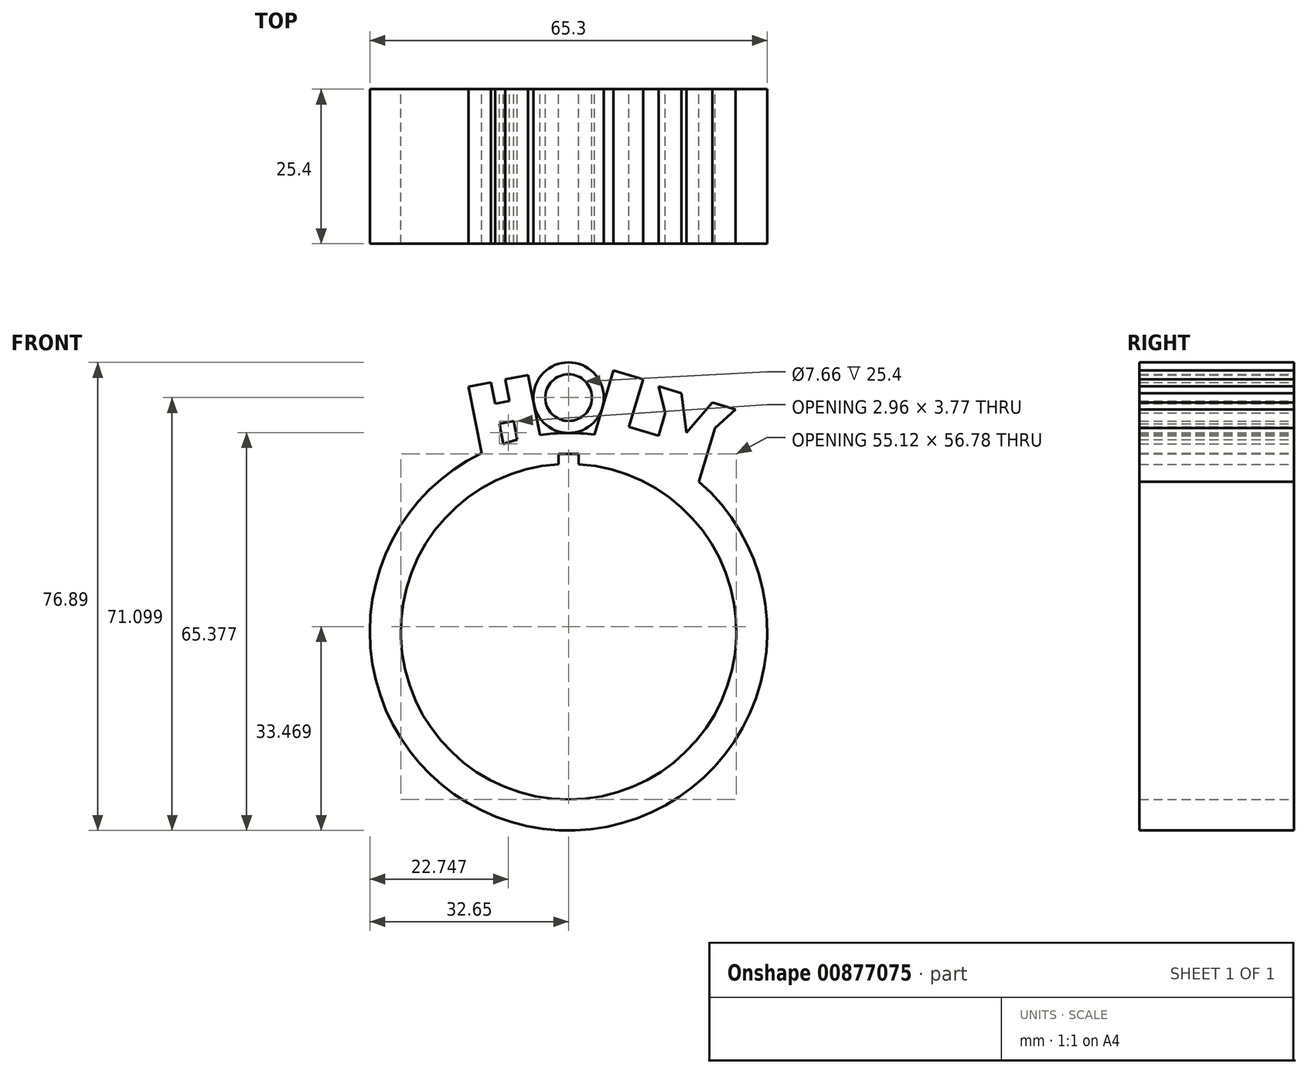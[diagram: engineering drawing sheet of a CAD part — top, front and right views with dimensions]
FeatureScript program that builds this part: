
annotation { "Feature Type Name" : "Feature", "Feature Type Description" : "" }
export const myFeature = defineFeature(function(context is Context, id is Id, definition is map)
    precondition{}
    {
        {
            var Q0;
            Q0=qCreatedBy(makeId("Front.planeOp"),FACE);
            var sketch = newSketch(context, id + "F0", { "sketchPlane" : qUnion([Q0])});
            skLineSegment(sketch, "E0", {"start": v(0, -38.5) * mm, "end": v(0, 44.83) * mm, "construction": true});
            skCircle(sketch, "E1", {"center": v(0, 0) * mm, "radius": 27.57 * mm});
            skArc(sketch, "E2", {"start": v(17.77, 27.4) * mm, "mid": v(-18.57, -26.86) * mm, "end": v(19.34, 26.3) * mm});
            skLineSegment(sketch, "E3", {"start": v(-16.47, 40.24) * mm, "end": v(-14.31, 29.35) * mm});
            skLineSegment(sketch, "E4", {"start": v(-16.47, 40.24) * mm, "end": v(-12.74, 40.98) * mm});
            skLineSegment(sketch, "E5", {"start": v(-12.74, 40.98) * mm, "end": v(-12.04, 37.45) * mm});
            skLineSegment(sketch, "E6", {"start": v(-12.04, 37.45) * mm, "end": v(-9.69, 37.92) * mm});
            skLineSegment(sketch, "E7", {"start": v(-9.69, 37.92) * mm, "end": v(-10.39, 41.44) * mm});
            skLineSegment(sketch, "E8", {"start": v(-10.39, 41.44) * mm, "end": v(-6.65, 42.18) * mm});
            skLineSegment(sketch, "E9", {"start": v(-6.65, 42.18) * mm, "end": v(-4.7, 32.31) * mm});
            skLineSegment(sketch, "E10", {"start": v(-11.38, 34.15) * mm, "end": v(-10.73, 30.84) * mm});
            skLineSegment(sketch, "E11", {"start": v(-11.38, 34.15) * mm, "end": v(-9.03, 34.61) * mm});
            skLineSegment(sketch, "E12", {"start": v(-9.03, 34.61) * mm, "end": v(-8.42, 31.55) * mm});
            skCircle(sketch, "E13", {"center": v(0, 38.45) * mm, "radius": 5.8 * mm});
            skCircle(sketch, "E14", {"center": v(0, 38.45) * mm, "radius": 3.83 * mm});
            skLineSegment(sketch, "E15", {"start": v(7.4, 42.9) * mm, "end": v(4.22, 32.38) * mm});
            skLineSegment(sketch, "E16", {"start": v(7.4, 42.9) * mm, "end": v(12.26, 41.43) * mm});
            skLineSegment(sketch, "E17", {"start": v(12.26, 41.43) * mm, "end": v(9.92, 33.67) * mm});
            skLineSegment(sketch, "E18", {"start": v(9.92, 33.67) * mm, "end": v(14.78, 32.2) * mm});
            skLineSegment(sketch, "E19", {"start": v(14.78, 32.2) * mm, "end": v(13.97, 29.51) * mm});
            skLineSegment(sketch, "E20", {"start": v(17.77, 27.4) * mm, "end": v(19.34, 26.3) * mm});
            skLineSegment(sketch, "E21", {"start": v(14.78, 32.2) * mm, "end": v(15.9, 35.9) * mm});
            skLineSegment(sketch, "E22", {"start": v(15.9, 35.9) * mm, "end": v(14.78, 40.33) * mm});
            skLineSegment(sketch, "E23", {"start": v(14.78, 40.33) * mm, "end": v(18.55, 39.2) * mm});
            skLineSegment(sketch, "E24", {"start": v(18.55, 39.2) * mm, "end": v(19.37, 32.67) * mm});
            skLineSegment(sketch, "E25", {"start": v(19.37, 32.67) * mm, "end": v(17.77, 27.4) * mm, "construction": true});
            skLineSegment(sketch, "E26.MirrorCS", {"start": v(22.93, 29.75) * mm, "end": v(24.04, 33.46) * mm});
            skLineSegment(sketch, "E27.MirrorCS", {"start": v(23.64, 37.66) * mm, "end": v(19.37, 32.67) * mm});
            skLineSegment(sketch, "E28.MirrorCS", {"start": v(27.41, 36.53) * mm, "end": v(23.64, 37.66) * mm});
            skLineSegment(sketch, "E29.MirrorCS", {"start": v(24.04, 33.46) * mm, "end": v(27.41, 36.53) * mm});
            skLineSegment(sketch, "E30", {"start": v(22.93, 29.75) * mm, "end": v(21.4, 24.67) * mm});
            skLineSegment(sketch, "E31", {"start": v(0, 29.2) * mm, "end": v(1.64, 29.2) * mm});
            skLineSegment(sketch, "E32", {"start": v(1.64, 29.2) * mm, "end": v(1.64, 27.52) * mm});
            skLineSegment(sketch, "E33.MirrorCS", {"start": v(-1.64, 29.2) * mm, "end": v(-1.64, 27.52) * mm});
            skLineSegment(sketch, "E34.MirrorCS", {"start": v(0, 29.2) * mm, "end": v(-1.64, 29.2) * mm});
            skSolve(sketch);
        }
        {
            var Q0;
            {var subQ0=sQuery(id+"F0.wireOp",EDGE,"E20");Q0=makeQuery(id+"F0.imprint","IMPRINT",FACE,{"disambiguationData":[TD([[makeQuery(id+"F0.imprint","IMPRINT",EDGE,{"derivedFrom":subQ0}),-1.0]])]});}
            var Q1;
            {var subQ3=sQuery(id+"F0.wireOp",EDGE,"E19");Q1=makeQuery(id+"F0.imprint","IMPRINT",FACE,{"disambiguationData":[TD([[makeQuery(id+"F0.imprint","IMPRINT",EDGE,{"derivedFrom":subQ3}),1.0]])]});}
            var Q2;
            {var subQ4=sQuery(id+"F0.wireOp",EDGE,"E16");Q2=makeQuery(id+"F0.imprint","IMPRINT",FACE,{"disambiguationData":[TD([[makeQuery(id+"F0.imprint","IMPRINT",EDGE,{"derivedFrom":subQ4}),-1.0]])]});}
            var Q3;
            Q3=makeQuery(id+"F0.imprint","IMPRINT",FACE,{"disambiguationData":[TD([[makeQuery(id+"F0.imprint","IMPRINT",EDGE,{"derivedFrom":sQuery(id+"F0.wireOp",EDGE,"E14")}),-1.0]])]});
            var Q4;
            {var subQ6=sQuery(id+"F0.wireOp",EDGE,"E3");Q4=makeQuery(id+"F0.imprint","IMPRINT",FACE,{"disambiguationData":[TD([[makeQuery(id+"F0.imprint","IMPRINT",EDGE,{"derivedFrom":subQ6}),1.0]])]});}
            extrude(context, id + "F1", {"entities" : qUnion([Q0, Q1, Q2, Q3, Q4]), "depth" : 25.4 * mm, "offsetDistance" : 25.4 * mm});
        }
    });
